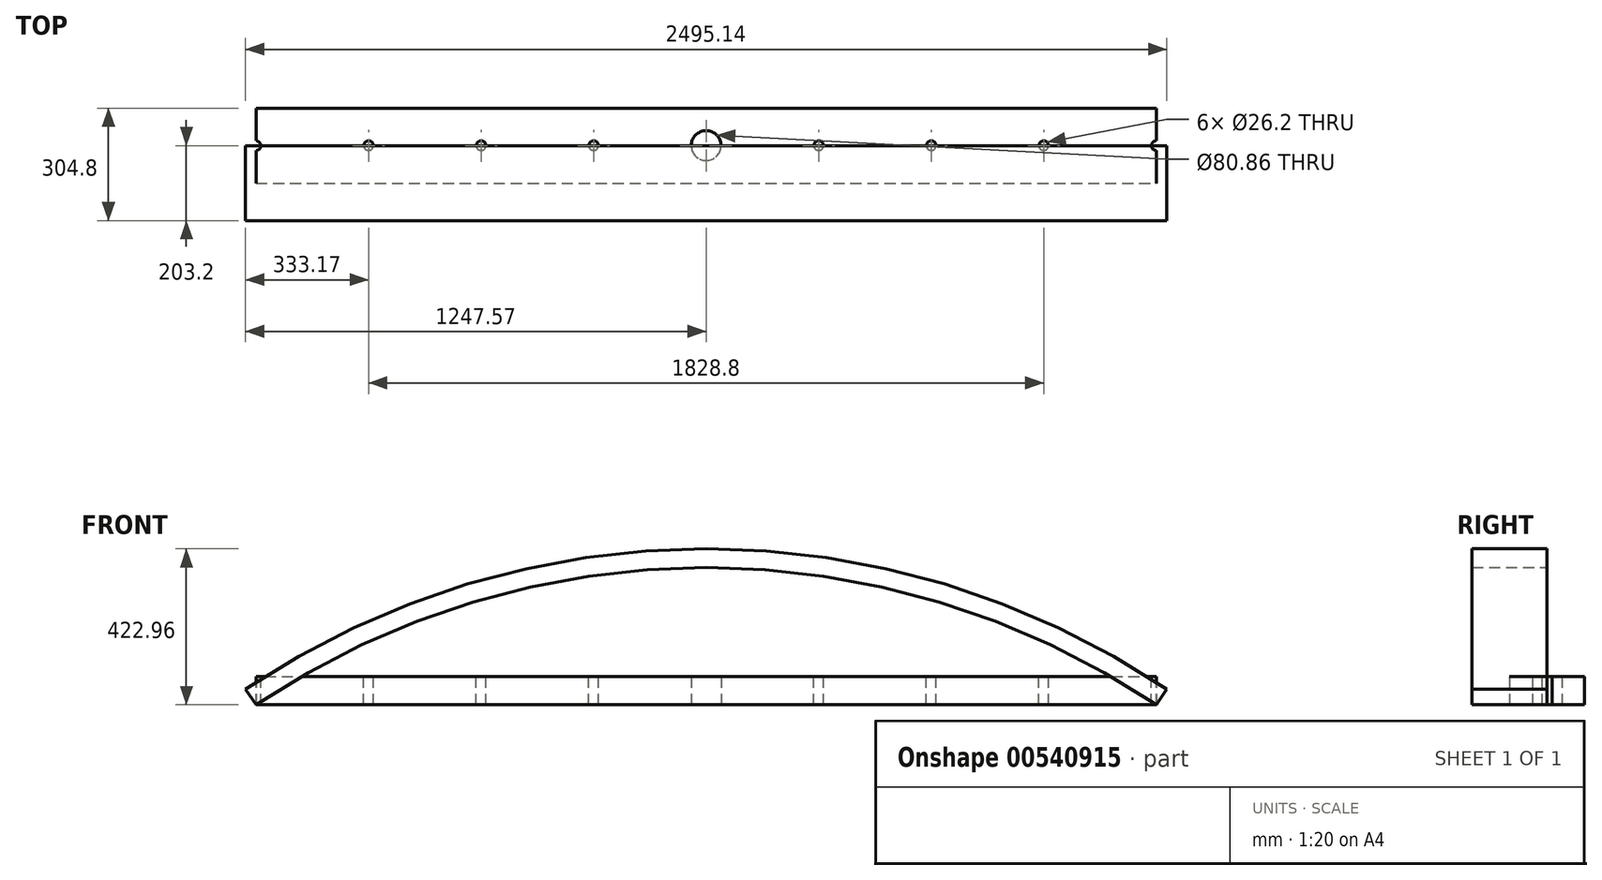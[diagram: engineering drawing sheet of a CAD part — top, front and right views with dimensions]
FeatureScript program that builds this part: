
annotation { "Feature Type Name" : "Feature", "Feature Type Description" : "" }
export const myFeature = defineFeature(function(context is Context, id is Id, definition is map)
    precondition{}
    {
        {
            var Q0;
            Q0=qCreatedBy(makeId("Front.planeOp"),FACE);
            var sketch = newSketch(context, id + "F0", { "sketchPlane" : qUnion([Q0])});
            skPoint(sketch, "E0.end.orphan", {"position": v(-1219.2, 0) * mm});
            skPoint(sketch, "E0.start.orphan", {"position": v(1219.2, 0) * mm});
            skArc(sketch, "E1", {"start": v(1219.2, 0) * mm, "mid": v(0, 372.16) * mm, "end": v(-1219.2, 0) * mm});
            skArc(sketch, "E2.0", {"start": v(1247.57, 42.14) * mm, "mid": v(0, 422.96) * mm, "end": v(-1247.57, 42.14) * mm});
            skLineSegment(sketch, "E3", {"start": v(-1247.57, 42.14) * mm, "end": v(-1219.2, 0) * mm});
            skLineSegment(sketch, "E4", {"start": v(1247.57, 42.14) * mm, "end": v(1219.2, 0) * mm});
            skSolve(sketch);
        }
        {
            var Q0;
            Q0 = qSketchRegion(id + "F0", true);
            extrude(context, id + "F1", {"entities" : qUnion([Q0]), "depth" : 203.2 * mm, "offsetDistance" : 25.4 * mm});
        }
        {
            var Q0;
            Q0=qCreatedBy(makeId("Right.planeOp"),FACE);
            var sketch = newSketch(context, id + "F2", { "sketchPlane" : qUnion([Q0])});
            skLineSegment(sketch, "E5", {"start": v(-203.2, 422.96) * mm, "end": v(0, 422.96) * mm});
            skPoint(sketch, "E6", {"position": v(-101.6, 422.96) * mm});
            skSolve(sketch);
        }
        {
            var Q0;
            Q0=qCreatedBy(makeId("Top.planeOp"),FACE);
            var Q1;
            Q1=sQuery(id+"F2.wireOp",VERTEX,"E6");
            cPlane(context, id + "F3", {"entities" : qUnion([Q0, Q1]), "cplaneType" : CPlaneType.PLANE_POINT, "offset" : 25.4 * mm, "width" : 152.4 * mm, "height" : 152.4 * mm});
        }
        {
            var Q0;
            Q0=qCreatedBy(id+"F3.planeOp",FACE);
            var sketch = newSketch(context, id + "F4", { "sketchPlane" : qUnion([Q0])});
            skCircle(sketch, "E7", {"center": v(0, -102.56) * mm, "radius": 22.42 * mm});
            skSolve(sketch);
        }
        {
            var Q0;
            Q0=qCreatedBy(makeId("Top.planeOp"),FACE);
            var sketch = newSketch(context, id + "F5", { "sketchPlane" : qUnion([Q0])});
            skLineSegment(sketch, "E8.bottom", {"start": v(-1219.2, 101.6) * mm, "end": v(1219.2, 101.6) * mm});
            skLineSegment(sketch, "E8.top", {"start": v(-1219.2, -101.6) * mm, "end": v(1219.2, -101.6) * mm});
            skLineSegment(sketch, "E8.left", {"start": v(-1219.2, 101.6) * mm, "end": v(-1219.2, -101.6) * mm});
            skLineSegment(sketch, "E8.right", {"start": v(1219.2, 101.6) * mm, "end": v(1219.2, -101.6) * mm});
            skPoint(sketch, "E8.middle", {"position": v(0, 0) * mm});
            skCircle(sketch, "E9", {"center": v(0, 0) * mm, "radius": 40.43 * mm});
            skLineSegment(sketch, "E10", {"start": v(-1219.2, 0) * mm, "end": v(1219.2, 0) * mm, "construction": true});
            skLineSegment(sketch, "E11", {"start": v(304.8, 101.6) * mm, "end": v(304.8, -101.6) * mm, "construction": true});
            skLineSegment(sketch, "E12", {"start": v(609.6, 101.6) * mm, "end": v(609.6, -101.6) * mm, "construction": true});
            skLineSegment(sketch, "E13", {"start": v(914.4, 101.6) * mm, "end": v(914.4, -101.6) * mm, "construction": true});
            skLineSegment(sketch, "E14", {"start": v(1219.2, 101.6) * mm, "end": v(1219.2, -101.6) * mm, "construction": true});
            skLineSegment(sketch, "E15.MirrorCS", {"start": v(-304.8, 101.6) * mm, "end": v(-304.8, -101.6) * mm, "construction": true});
            skLineSegment(sketch, "E16.MirrorCS", {"start": v(-609.6, 101.6) * mm, "end": v(-609.6, -101.6) * mm, "construction": true});
            skLineSegment(sketch, "E17.MirrorCS", {"start": v(-914.4, 101.6) * mm, "end": v(-914.4, -101.6) * mm, "construction": true});
            skLineSegment(sketch, "E18.MirrorCS", {"start": v(-1219.2, 101.6) * mm, "end": v(-1219.2, -101.6) * mm, "construction": true});
            skPoint(sketch, "E19", {"position": v(-1219.2, 0) * mm});
            skPoint(sketch, "E20", {"position": v(-914.4, 0) * mm});
            skPoint(sketch, "E21", {"position": v(-609.6, 0) * mm});
            skPoint(sketch, "E22", {"position": v(-304.8, 0) * mm});
            skPoint(sketch, "E23", {"position": v(304.8, 0) * mm});
            skPoint(sketch, "E24", {"position": v(609.6, 0) * mm});
            skPoint(sketch, "E25", {"position": v(914.4, 0) * mm});
            skPoint(sketch, "E26", {"position": v(1219.2, 0) * mm});
            skSolve(sketch);
        }
        {
            var Q0;
            Q0 = qSketchRegion(id + "F5", true);
            extrude(context, id + "F6", {"entities" : qUnion([Q0]), "depth" : 76.2 * mm, "offsetDistance" : 25.4 * mm});
        }
        {
            var Q0;
            Q0=sQuery(id+"F5.wireOp",VERTEX,"E20");
            var Q1;
            Q1=makeQuery(id+"F6.opExtrude","SWEPT_BODY",BODY,{"disambiguationData":[OSD([sQuery(id+"F5.wireOp",EDGE,"E8.bottom"),sQuery(id+"F5.wireOp",EDGE,"E8.top"),sQuery(id+"F5.wireOp",EDGE,"E8.left"),sQuery(id+"F5.wireOp",EDGE,"E8.right"),sQuery(id+"F5.wireOp",EDGE,"E9")])]});
            hole(context, id + "F7", {"style" : HoleStyle.SIMPLE, "endStyle" : HoleEndStyle.THROUGH, "oppositeDirection" : true, "standardTappedOrClearance" : lookupTablePath({ "standard" : "ANSI", "fit" : "Normal (ASME)", "size" : "1", "type" : "Clearance" }), "standardBlindInLast" : lookupTablePath({ "fit" : "Free", "standard" : "ANSI", "size" : "1", "type" : "Clearance" }), "holeDiameter" : 26.2 * mm, "isTappedThrough" : true, "tappedDepth" : 12.7 * mm, "tapClearance" : 3, "startFromSketch" : true, "locations" : qUnion([Q0]), "scope" : qUnion([Q1])});
        }
        {
            var Q0;
            Q0=sQuery(id+"F5.wireOp",VERTEX,"E21");
            var Q1;
            Q1=makeQuery(id+"F6.opExtrude","SWEPT_BODY",BODY,{"disambiguationData":[OSD([sQuery(id+"F5.wireOp",EDGE,"E8.bottom"),sQuery(id+"F5.wireOp",EDGE,"E8.top"),sQuery(id+"F5.wireOp",EDGE,"E8.left"),sQuery(id+"F5.wireOp",EDGE,"E8.right"),sQuery(id+"F5.wireOp",EDGE,"E9")])]});
            hole(context, id + "F8", {"style" : HoleStyle.SIMPLE, "endStyle" : HoleEndStyle.THROUGH, "oppositeDirection" : true, "standardTappedOrClearance" : lookupTablePath({ "standard" : "ANSI", "fit" : "Normal (ASME)", "size" : "1", "type" : "Clearance" }), "standardBlindInLast" : lookupTablePath({ "fit" : "Free", "standard" : "ANSI", "size" : "1", "type" : "Clearance" }), "holeDiameter" : 26.2 * mm, "isTappedThrough" : true, "tappedDepth" : 12.7 * mm, "tapClearance" : 3, "startFromSketch" : true, "locations" : qUnion([Q0]), "scope" : qUnion([Q1])});
        }
        {
            var Q0;
            Q0=sQuery(id+"F5.wireOp",VERTEX,"E22");
            var Q1;
            Q1=makeQuery(id+"F6.opExtrude","SWEPT_BODY",BODY,{"disambiguationData":[OSD([sQuery(id+"F5.wireOp",EDGE,"E8.bottom"),sQuery(id+"F5.wireOp",EDGE,"E8.top"),sQuery(id+"F5.wireOp",EDGE,"E8.left"),sQuery(id+"F5.wireOp",EDGE,"E8.right"),sQuery(id+"F5.wireOp",EDGE,"E9")])]});
            hole(context, id + "F9", {"style" : HoleStyle.SIMPLE, "endStyle" : HoleEndStyle.THROUGH, "oppositeDirection" : true, "standardTappedOrClearance" : lookupTablePath({ "standard" : "ANSI", "fit" : "Normal (ASME)", "size" : "1", "type" : "Clearance" }), "standardBlindInLast" : lookupTablePath({ "fit" : "Free", "standard" : "ANSI", "size" : "1", "type" : "Clearance" }), "holeDiameter" : 26.2 * mm, "isTappedThrough" : true, "tappedDepth" : 12.7 * mm, "tapClearance" : 3, "startFromSketch" : true, "locations" : qUnion([Q0]), "scope" : qUnion([Q1])});
        }
        {
            var Q0;
            Q0=sQuery(id+"F5.wireOp",VERTEX,"E23");
            var Q1;
            Q1=makeQuery(id+"F6.opExtrude","SWEPT_BODY",BODY,{"disambiguationData":[OSD([sQuery(id+"F5.wireOp",EDGE,"E8.bottom"),sQuery(id+"F5.wireOp",EDGE,"E8.top"),sQuery(id+"F5.wireOp",EDGE,"E8.left"),sQuery(id+"F5.wireOp",EDGE,"E8.right"),sQuery(id+"F5.wireOp",EDGE,"E9")])]});
            hole(context, id + "F10", {"style" : HoleStyle.SIMPLE, "endStyle" : HoleEndStyle.THROUGH, "oppositeDirection" : true, "standardTappedOrClearance" : lookupTablePath({ "standard" : "ANSI", "fit" : "Normal (ASME)", "size" : "1", "type" : "Clearance" }), "standardBlindInLast" : lookupTablePath({ "fit" : "Free", "standard" : "ANSI", "size" : "1", "type" : "Clearance" }), "holeDiameter" : 26.2 * mm, "isTappedThrough" : true, "tappedDepth" : 12.7 * mm, "tapClearance" : 3, "startFromSketch" : true, "locations" : qUnion([Q0]), "scope" : qUnion([Q1])});
        }
        {
            var Q0;
            Q0=sQuery(id+"F5.wireOp",VERTEX,"E24");
            var Q1;
            Q1=makeQuery(id+"F6.opExtrude","SWEPT_BODY",BODY,{"disambiguationData":[OSD([sQuery(id+"F5.wireOp",EDGE,"E8.bottom"),sQuery(id+"F5.wireOp",EDGE,"E8.top"),sQuery(id+"F5.wireOp",EDGE,"E8.left"),sQuery(id+"F5.wireOp",EDGE,"E8.right"),sQuery(id+"F5.wireOp",EDGE,"E9")])]});
            hole(context, id + "F11", {"style" : HoleStyle.SIMPLE, "endStyle" : HoleEndStyle.THROUGH, "oppositeDirection" : true, "standardTappedOrClearance" : lookupTablePath({ "standard" : "ANSI", "fit" : "Normal (ASME)", "size" : "1", "type" : "Clearance" }), "standardBlindInLast" : lookupTablePath({ "fit" : "Free", "standard" : "ANSI", "size" : "1", "type" : "Clearance" }), "holeDiameter" : 26.2 * mm, "isTappedThrough" : true, "tappedDepth" : 12.7 * mm, "tapClearance" : 3, "startFromSketch" : true, "locations" : qUnion([Q0]), "scope" : qUnion([Q1])});
        }
        {
            var Q0;
            Q0=sQuery(id+"F5.wireOp",VERTEX,"E25");
            var Q1;
            Q1=makeQuery(id+"F6.opExtrude","SWEPT_BODY",BODY,{"disambiguationData":[OSD([sQuery(id+"F5.wireOp",EDGE,"E8.bottom"),sQuery(id+"F5.wireOp",EDGE,"E8.top"),sQuery(id+"F5.wireOp",EDGE,"E8.left"),sQuery(id+"F5.wireOp",EDGE,"E8.right"),sQuery(id+"F5.wireOp",EDGE,"E9")])]});
            hole(context, id + "F12", {"style" : HoleStyle.SIMPLE, "endStyle" : HoleEndStyle.THROUGH, "oppositeDirection" : true, "standardTappedOrClearance" : lookupTablePath({ "standard" : "ANSI", "fit" : "Normal (ASME)", "size" : "1", "type" : "Clearance" }), "standardBlindInLast" : lookupTablePath({ "fit" : "Free", "standard" : "ANSI", "size" : "1", "type" : "Clearance" }), "holeDiameter" : 26.2 * mm, "isTappedThrough" : true, "tappedDepth" : 12.7 * mm, "tapClearance" : 3, "startFromSketch" : true, "locations" : qUnion([Q0]), "scope" : qUnion([Q1])});
        }
        {
            var Q0;
            Q0=sQuery(id+"F5.wireOp",VERTEX,"E26");
            var Q1;
            Q1=makeQuery(id+"F6.opExtrude","SWEPT_BODY",BODY,{"disambiguationData":[OSD([sQuery(id+"F5.wireOp",EDGE,"E8.bottom"),sQuery(id+"F5.wireOp",EDGE,"E8.top"),sQuery(id+"F5.wireOp",EDGE,"E8.left"),sQuery(id+"F5.wireOp",EDGE,"E8.right"),sQuery(id+"F5.wireOp",EDGE,"E9")])]});
            hole(context, id + "F13", {"style" : HoleStyle.SIMPLE, "endStyle" : HoleEndStyle.THROUGH, "oppositeDirection" : true, "standardTappedOrClearance" : lookupTablePath({ "standard" : "ANSI", "fit" : "Normal (ASME)", "size" : "1", "type" : "Clearance" }), "standardBlindInLast" : lookupTablePath({ "fit" : "Free", "standard" : "ANSI", "size" : "1", "type" : "Clearance" }), "holeDiameter" : 26.2 * mm, "isTappedThrough" : true, "tappedDepth" : 12.7 * mm, "tapClearance" : 3, "startFromSketch" : true, "locations" : qUnion([Q0]), "scope" : qUnion([Q1])});
        }
        {
            var Q0;
            Q0=sQuery(id+"F5.wireOp",VERTEX,"E19");
            var Q1;
            Q1=makeQuery(id+"F6.opExtrude","SWEPT_BODY",BODY,{"disambiguationData":[OSD([sQuery(id+"F5.wireOp",EDGE,"E8.bottom"),sQuery(id+"F5.wireOp",EDGE,"E8.top"),sQuery(id+"F5.wireOp",EDGE,"E8.left"),sQuery(id+"F5.wireOp",EDGE,"E8.right"),sQuery(id+"F5.wireOp",EDGE,"E9")])]});
            hole(context, id + "F14", {"style" : HoleStyle.SIMPLE, "endStyle" : HoleEndStyle.THROUGH, "oppositeDirection" : true, "standardTappedOrClearance" : lookupTablePath({ "standard" : "ANSI", "fit" : "Normal (ASME)", "size" : "1", "type" : "Clearance" }), "standardBlindInLast" : lookupTablePath({ "fit" : "Free", "standard" : "ANSI", "size" : "1", "type" : "Clearance" }), "holeDiameter" : 26.2 * mm, "isTappedThrough" : true, "tappedDepth" : 12.7 * mm, "tapClearance" : 3, "startFromSketch" : true, "locations" : qUnion([Q0]), "scope" : qUnion([Q1])});
        }
    });
